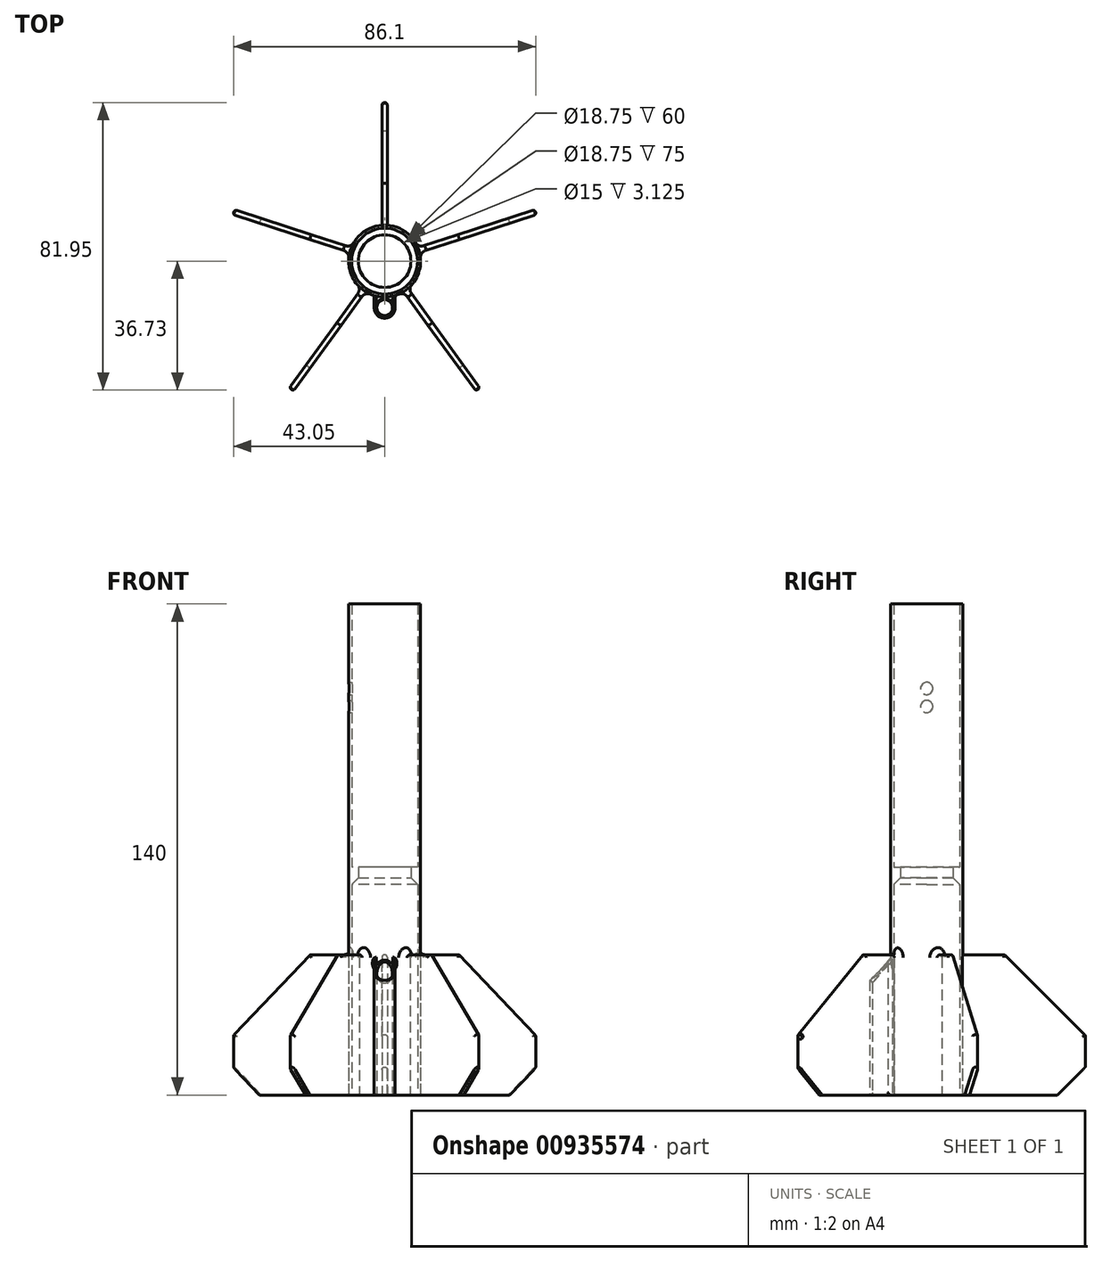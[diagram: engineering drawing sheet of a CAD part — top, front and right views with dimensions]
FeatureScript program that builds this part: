
annotation { "Feature Type Name" : "Feature", "Feature Type Description" : "" }
export const myFeature = defineFeature(function(context is Context, id is Id, definition is map)
    precondition{}
    {
        {
            var Q0;
            Q0=qCreatedBy(makeId("Top.planeOp"),FACE);
            var sketch = newSketch(context, id + "F0", { "sketchPlane" : qUnion([Q0])});
            skCircle(sketch, "E0", {"center": v(0, 0) * mm, "radius": 9.38 * mm});
            skCircle(sketch, "E1", {"center": v(0, 0) * mm, "radius": 10.25 * mm});
            skCircle(sketch, "E2", {"center": v(0, -13.25) * mm, "radius": 2.25 * mm});
            skCircle(sketch, "E3", {"center": v(0, -13.25) * mm, "radius": 3 * mm});
            skLineSegment(sketch, "E4", {"start": v(-3, -13.25) * mm, "end": v(-3, -9.8) * mm});
            skLineSegment(sketch, "E5", {"start": v(3, -13.25) * mm, "end": v(3, -9.8) * mm});
            skLineSegment(sketch, "E6.bottom", {"start": v(-0.75, 45.22) * mm, "end": v(0.75, 45.22) * mm});
            skLineSegment(sketch, "E6.top", {"start": v(-0.75, 10.22) * mm, "end": v(0.75, 10.22) * mm, "construction": true});
            skLineSegment(sketch, "E6.left", {"start": v(-0.75, 45.22) * mm, "end": v(-0.75, 10.22) * mm});
            skLineSegment(sketch, "E6.right", {"start": v(0.75, 45.22) * mm, "end": v(0.75, 10.22) * mm});
            skCircle(sketch, "E7", {"center": v(0, 0) * mm, "radius": 7.5 * mm});
            skSolve(sketch);
        }
        {
            var Q0;
            Q0=makeQuery(id+"F0.imprint","IMPRINT",FACE,{"disambiguationData":[TD([[makeQuery(id+"F0.imprint","IMPRINT",EDGE,{"derivedFrom":sQuery(id+"F0.wireOp",EDGE,"E0")}),-1.0]])]});
            extrude(context, id + "F1", {"entities" : qUnion([Q0]), "depth" : 140 * mm, "offsetDistance" : 25 * mm});
        }
        {
            var Q0;
            Q0=makeQuery(id+"F0.imprint","IMPRINT",FACE,{"disambiguationData":[TD([[makeQuery(id+"F0.imprint","IMPRINT",EDGE,{"derivedFrom":sQuery(id+"F0.wireOp",EDGE,"E6.bottom")}),-1.0]])]});
            extrude(context, id + "F2", {"entities" : qUnion([Q0]), "operationType" : NewBodyOperationType.ADD, "depth" : 40 * mm, "offsetDistance" : 25 * mm});
        }
        {
            var Q0;
            Q0=makeQuery(id+"F2.opExtrude","CAP_EDGE",EDGE,{"disambiguationData":[OSD([sQuery(id+"F0.wireOp",EDGE,"E6.bottom")])],"isStart":false});
            chamfer(context, id + "F3", {"entities" : qUnion([Q0]), "width" : 23 * mm, "tangentPropagation" : true});
        }
        {
            var Q0;
            Q0=makeQuery(id+"F2.opExtrude","CAP_EDGE",EDGE,{"disambiguationData":[OSD([sQuery(id+"F0.wireOp",EDGE,"E6.right")])],"isStart":false});
            var Q1;
            Q1=makeQuery(id+"F2.opExtrude","CAP_EDGE",EDGE,{"disambiguationData":[OSD([sQuery(id+"F0.wireOp",EDGE,"E6.left")])],"isStart":false});
            var Q2;
            Q2=makeQuery(id+"F3.opChamfer","BLEND_EDGE",EDGE,{"blendedFrom":[makeQuery(id+"F2.opExtrude","CAP_EDGE",EDGE,{"disambiguationData":[OSD([sQuery(id+"F0.wireOp",EDGE,"E6.bottom")])],"isStart":false}),makeQuery(id+"F2.opExtrude","SWEPT_FACE",FACE,{"disambiguationData":[OSD([sQuery(id+"F0.wireOp",EDGE,"E6.right")])]})],"blendedInto":[makeQuery(id+"F2.opExtrude","SWEPT_FACE",FACE,{"disambiguationData":[OSD([sQuery(id+"F0.wireOp",EDGE,"E6.right")])]})]});
            var Q3;
            Q3=makeQuery(id+"F3.opChamfer","BLEND_EDGE",EDGE,{"blendedFrom":[makeQuery(id+"F2.opExtrude","CAP_EDGE",EDGE,{"disambiguationData":[OSD([sQuery(id+"F0.wireOp",EDGE,"E6.bottom")])],"isStart":false}),makeQuery(id+"F2.opExtrude","SWEPT_FACE",FACE,{"disambiguationData":[OSD([sQuery(id+"F0.wireOp",EDGE,"E6.left")])]})],"blendedInto":[makeQuery(id+"F2.opExtrude","SWEPT_FACE",FACE,{"disambiguationData":[OSD([sQuery(id+"F0.wireOp",EDGE,"E6.left")])]})]});
            fillet(context, id + "F4", {"entities" : qUnion([Q0, Q1, Q2, Q3]), "radius" : .75 * mm, "tangentPropagation" : true, "allowEdgeOverflow" : false});
        }
        {
            var Q0;
            Q0=makeQuery(id+"F1.opExtrude","SWEPT_BODY",BODY,{"disambiguationData":[OSD([sQuery(id+"F0.wireOp",EDGE,"E0"),sQuery(id+"F0.wireOp",EDGE,"E1")])]});
            var Q1;
            Q1=sQuery(id+"F0.wireOp",EDGE,"E1");
            circularPattern(context, id + "F5", {"entities" : qUnion([Q0]), "axis" : qUnion([Q1]), "angle" : 360 * degree, "instanceCount" : 5, "oppositeDirection" : true, "equalSpace" : true});
        }
        {
            var Q0;
            {var subQ0=sQuery(id+"F0.wireOp",EDGE,"E5");Q0=makeQuery(id+"F0.imprint","IMPRINT",FACE,{"disambiguationData":[TD([[makeQuery(id+"F0.imprint","IMPRINT",EDGE,{"derivedFrom":subQ0}),1.0]])]});}
            var Q1;
            Q1=makeQuery(id+"F0.imprint","IMPRINT",FACE,{"disambiguationData":[TD([[makeQuery(id+"F0.imprint","IMPRINT",EDGE,{"derivedFrom":sQuery(id+"F0.wireOp",EDGE,"E2")}),-1.0]])]});
            var Q2;
            {var subQ0=sQuery(id+"F0.wireOp",EDGE,"E4");Q2=makeQuery(id+"F0.imprint","IMPRINT",FACE,{"disambiguationData":[TD([[makeQuery(id+"F0.imprint","IMPRINT",EDGE,{"derivedFrom":subQ0}),-1.0]])]});}
            var Q3;
            Q3=sQuery(id+"F0.wireOp",EDGE,"E5");
            var Q4;
            Q4=sQuery(id+"F0.wireOp",EDGE,"E3");
            var Q5;
            Q5=sQuery(id+"F0.wireOp",EDGE,"E2");
            var Q6;
            Q6=sQuery(id+"F0.wireOp",EDGE,"E4");
            extrude(context, id + "F6", {"entities" : qUnion([Q0, Q1, Q2]), "operationType" : NewBodyOperationType.ADD, "surfaceEntities" : qUnion([Q3, Q4, Q5, Q6]), "depth" : 33 * mm, "offsetDistance" : 25 * mm});
        }
        {
            var Q0;
            {var subQ0=sQuery(id+"F0.wireOp",EDGE,"E1");var subQ1=makeQuery(id+"F1.opExtrude","SWEPT_FACE",FACE,{"disambiguationData":[OSD([subQ0])]});var subQ2=subQ1;Q0=makeQuery(id+"F6.boolean.opBoolean","INTERSECT",EDGE,{"disambiguationData":[topologyDisambiguationEdgeConnected([makeQuery(id+"F6.opExtrude","CAP_FACE",FACE,{"disambiguationData":[OSD([subQ0,sQuery(id+"F0.wireOp",EDGE,"E2"),sQuery(id+"F0.wireOp",EDGE,"E3"),sQuery(id+"F0.wireOp",EDGE,"E4"),sQuery(id+"F0.wireOp",EDGE,"E5")])],"isStart":false})])],"derivedFrom":[subQ2,makeQuery(id+"F5.opPattern","COPY",FACE,{"derivedFrom":subQ2,"instanceName":"1"}),makeQuery(id+"F5.opPattern","COPY",FACE,{"derivedFrom":subQ2,"instanceName":"2"}),makeQuery(id+"F5.opPattern","COPY",FACE,{"derivedFrom":subQ2,"instanceName":"3"}),makeQuery(id+"F5.opPattern","COPY",FACE,{"derivedFrom":subQ2,"instanceName":"4"})]});}
            chamfer(context, id + "F7", {"entities" : qUnion([Q0]), "width" : 6 * mm, "tangentPropagation" : true});
        }
        {
            var Q0;
            Q0=makeQuery(id+"F7.opChamfer","BLEND_FACE",FACE,{"disambiguationData":[OSD([sQuery(id+"F0.wireOp",EDGE,"E1")])]});
            fillet(context, id + "F8", {"entities" : qUnion([Q0]), "radius" : .75 * mm, "tangentPropagation" : true, "allowEdgeOverflow" : false});
        }
        {
            var Q0;
            Q0=makeQuery(id+"F2.opExtrude","CAP_EDGE",EDGE,{"disambiguationData":[OSD([sQuery(id+"F0.wireOp",EDGE,"E6.bottom")])],"isStart":true});
            var Q1;
            Q1=makeQuery(id+"F5.opPattern","COPY",EDGE,{"derivedFrom":makeQuery(id+"F2.opExtrude","CAP_EDGE",EDGE,{"disambiguationData":[OSD([sQuery(id+"F0.wireOp",EDGE,"E6.bottom")])],"isStart":true}),"instanceName":"4"});
            var Q2;
            Q2=makeQuery(id+"F5.opPattern","COPY",EDGE,{"derivedFrom":makeQuery(id+"F2.opExtrude","CAP_EDGE",EDGE,{"disambiguationData":[OSD([sQuery(id+"F0.wireOp",EDGE,"E6.bottom")])],"isStart":true}),"instanceName":"3"});
            var Q3;
            Q3=makeQuery(id+"F5.opPattern","COPY",EDGE,{"derivedFrom":makeQuery(id+"F2.opExtrude","CAP_EDGE",EDGE,{"disambiguationData":[OSD([sQuery(id+"F0.wireOp",EDGE,"E6.bottom")])],"isStart":true}),"instanceName":"1"});
            var Q4;
            Q4=makeQuery(id+"F5.opPattern","COPY",EDGE,{"derivedFrom":makeQuery(id+"F2.opExtrude","CAP_EDGE",EDGE,{"disambiguationData":[OSD([sQuery(id+"F0.wireOp",EDGE,"E6.bottom")])],"isStart":true}),"instanceName":"2"});
            chamfer(context, id + "F9", {"entities" : qUnion([Q0, Q1, Q2, Q3, Q4]), "width" : 8 * mm, "tangentPropagation" : true});
        }
        {
            var Q0;
            Q0=makeQuery(id+"F5.opPattern","COPY",EDGE,{"derivedFrom":makeQuery(id+"F2.opExtrude","SWEPT_EDGE",EDGE,{"disambiguationData":[OSD([sQuery(id+"F0.wireOp",EDGE,"E6.bottom"),sQuery(id+"F0.wireOp",EDGE,"E6.right")])]}),"instanceName":"1"});
            var Q1;
            Q1=makeQuery(id+"F5.opPattern","COPY",EDGE,{"derivedFrom":makeQuery(id+"F2.opExtrude","SWEPT_EDGE",EDGE,{"disambiguationData":[OSD([sQuery(id+"F0.wireOp",EDGE,"E6.bottom"),sQuery(id+"F0.wireOp",EDGE,"E6.right")])]}),"instanceName":"2"});
            var Q2;
            Q2=makeQuery(id+"F5.opPattern","COPY",EDGE,{"derivedFrom":makeQuery(id+"F2.opExtrude","SWEPT_EDGE",EDGE,{"disambiguationData":[OSD([sQuery(id+"F0.wireOp",EDGE,"E6.bottom"),sQuery(id+"F0.wireOp",EDGE,"E6.right")])]}),"instanceName":"3"});
            var Q3;
            Q3=makeQuery(id+"F5.opPattern","COPY",EDGE,{"derivedFrom":makeQuery(id+"F2.opExtrude","SWEPT_EDGE",EDGE,{"disambiguationData":[OSD([sQuery(id+"F0.wireOp",EDGE,"E6.bottom"),sQuery(id+"F0.wireOp",EDGE,"E6.right")])]}),"instanceName":"4"});
            var Q4;
            Q4=makeQuery(id+"F2.opExtrude","SWEPT_EDGE",EDGE,{"disambiguationData":[OSD([sQuery(id+"F0.wireOp",EDGE,"E6.bottom"),sQuery(id+"F0.wireOp",EDGE,"E6.right")])]});
            fillet(context, id + "F10", {"entities" : qUnion([Q0, Q1, Q2, Q3, Q4]), "radius" : .75 * mm, "tangentPropagation" : true, "allowEdgeOverflow" : false});
        }
        {
            var Q0;
            {var subQ0=makeQuery(id+"F1.opExtrude","SWEPT_FACE",FACE,{"disambiguationData":[OSD([sQuery(id+"F0.wireOp",EDGE,"E1")])]});var subQ1=subQ0;Q0=makeQuery(id+"F6.boolean.opBoolean","INTERSECT",EDGE,{"disambiguationData":[topologyDisambiguationEdgeConnected([makeQuery(id+"F5.opPattern","COPY",FACE,{"derivedFrom":makeQuery(id+"F2.opExtrude","SWEPT_FACE",FACE,{"disambiguationData":[OSD([sQuery(id+"F0.wireOp",EDGE,"E6.right")])]}),"instanceName":"2"})])],"derivedFrom":[subQ1,makeQuery(id+"F5.opPattern","COPY",FACE,{"derivedFrom":subQ1,"instanceName":"1"}),makeQuery(id+"F5.opPattern","COPY",FACE,{"derivedFrom":subQ1,"instanceName":"3"})]});}
            var Q1;
            {var subQ0=makeQuery(id+"F1.opExtrude","SWEPT_FACE",FACE,{"disambiguationData":[OSD([sQuery(id+"F0.wireOp",EDGE,"E1")])]});var subQ1=subQ0;Q1=makeQuery(id+"F6.boolean.opBoolean","INTERSECT",EDGE,{"disambiguationData":[topologyDisambiguationEdgeConnected([makeQuery(id+"F5.opPattern","COPY",FACE,{"derivedFrom":makeQuery(id+"F2.opExtrude","SWEPT_FACE",FACE,{"disambiguationData":[OSD([sQuery(id+"F0.wireOp",EDGE,"E6.right")])]}),"instanceName":"3"})])],"derivedFrom":[subQ1,makeQuery(id+"F5.opPattern","COPY",FACE,{"derivedFrom":subQ1,"instanceName":"1"}),makeQuery(id+"F5.opPattern","COPY",FACE,{"derivedFrom":subQ1,"instanceName":"2"}),makeQuery(id+"F5.opPattern","COPY",FACE,{"derivedFrom":subQ1,"instanceName":"4"})]});}
            var Q2;
            {var subQ0=makeQuery(id+"F1.opExtrude","SWEPT_FACE",FACE,{"disambiguationData":[OSD([sQuery(id+"F0.wireOp",EDGE,"E1")])]});var subQ1=subQ0;Q2=makeQuery(id+"F6.boolean.opBoolean","INTERSECT",EDGE,{"disambiguationData":[topologyDisambiguationEdgeConnected([makeQuery(id+"F5.opPattern","COPY",FACE,{"derivedFrom":makeQuery(id+"F2.opExtrude","SWEPT_FACE",FACE,{"disambiguationData":[OSD([sQuery(id+"F0.wireOp",EDGE,"E6.right")])]}),"instanceName":"4"})])],"derivedFrom":[subQ1,makeQuery(id+"F5.opPattern","COPY",FACE,{"derivedFrom":subQ1,"instanceName":"1"}),makeQuery(id+"F5.opPattern","COPY",FACE,{"derivedFrom":subQ1,"instanceName":"2"}),makeQuery(id+"F5.opPattern","COPY",FACE,{"derivedFrom":subQ1,"instanceName":"3"})]});}
            var Q3;
            Q3=makeQuery(id+"F2.opExtrude","SWEPT_EDGE",EDGE,{"disambiguationData":[OSD([sQuery(id+"F0.wireOp",EDGE,"E1"),sQuery(id+"F0.wireOp",EDGE,"E6.right")])]});
            var Q4;
            {var subQ0=makeQuery(id+"F1.opExtrude","SWEPT_FACE",FACE,{"disambiguationData":[OSD([sQuery(id+"F0.wireOp",EDGE,"E1")])]});var subQ1=subQ0;Q4=makeQuery(id+"F6.boolean.opBoolean","INTERSECT",EDGE,{"disambiguationData":[topologyDisambiguationEdgeConnected([makeQuery(id+"F5.opPattern","COPY",FACE,{"derivedFrom":makeQuery(id+"F2.opExtrude","SWEPT_FACE",FACE,{"disambiguationData":[OSD([sQuery(id+"F0.wireOp",EDGE,"E6.right")])]}),"instanceName":"1"})])],"derivedFrom":[subQ1,makeQuery(id+"F5.opPattern","COPY",FACE,{"derivedFrom":subQ1,"instanceName":"2"})]});}
            fillet(context, id + "F11", {"entities" : qUnion([Q0, Q1, Q2, Q3, Q4]), "radius" : 2 * mm, "tangentPropagation" : true, "allowEdgeOverflow" : false});
        }
        {
            var Q0;
            Q0=makeQuery(id+"F0.imprint","IMPRINT",FACE,{"disambiguationData":[TD([[makeQuery(id+"F0.imprint","IMPRINT",EDGE,{"derivedFrom":sQuery(id+"F0.wireOp",EDGE,"E0")}),1.0]])]});
            extrude(context, id + "F12", {"entities" : qUnion([Q0]), "operationType" : NewBodyOperationType.ADD, "depth" : 65 * mm, "offsetDistance" : 25 * mm, "hasSecondDirection" : true, "secondDirectionOppositeDirection" : false, "secondDirectionDepth" : 63 * mm});
        }
        {
            var Q0;
            Q0=makeQuery(id+"F12.opExtrude","CAP_EDGE",EDGE,{"disambiguationData":[OSD([sQuery(id+"F0.wireOp",EDGE,"E0")])],"isStart":true});
            chamfer(context, id + "F13", {"entities" : qUnion([Q0]), "width" : 3 * mm, "tangentPropagation" : true});
        }
        {
            var Q0;
            Q0=makeQuery(id+"F6.opExtrude","CAP_EDGE",EDGE,{"disambiguationData":[OSD([sQuery(id+"F0.wireOp",EDGE,"E2")])],"isStart":true});
            fillet(context, id + "F14", {"entities" : qUnion([Q0]), "radius" : .75 * mm, "tangentPropagation" : true, "allowEdgeOverflow" : false});
        }
        {
            var Q0;
            Q0=qCreatedBy(makeId("Right.planeOp"),FACE);
            var sketch = newSketch(context, id + "F15", { "sketchPlane" : qUnion([Q0])});
            skCircle(sketch, "E8", {"center": v(0, 115.91) * mm, "radius": 1.75 * mm});
            skCircle(sketch, "E9", {"center": v(0, 110.76) * mm, "radius": 1.75 * mm});
            skSolve(sketch);
        }
        {
            var Q0;
            Q0=makeQuery(id+"F15.imprint","IMPRINT",FACE,{"disambiguationData":[TD([[makeQuery(id+"F15.imprint","IMPRINT",EDGE,{"derivedFrom":sQuery(id+"F15.wireOp",EDGE,"E8")}),1.0]])]});
            var Q1;
            Q1=makeQuery(id+"F15.imprint","IMPRINT",FACE,{"disambiguationData":[TD([[makeQuery(id+"F15.imprint","IMPRINT",EDGE,{"derivedFrom":sQuery(id+"F15.wireOp",EDGE,"E9")}),1.0]])]});
            var Q2;
            Q2=sQuery(id+"F15.wireOp",EDGE,"E8");
            var Q3;
            Q3=sQuery(id+"F15.wireOp",EDGE,"E9");
            extrude(context, id + "F16", {"entities" : qUnion([Q0, Q1]), "operationType" : NewBodyOperationType.REMOVE, "surfaceEntities" : qUnion([Q2, Q3]), "oppositeDirection" : true, "depth" : 25 * mm, "offsetDistance" : 25 * mm});
        }
    });
